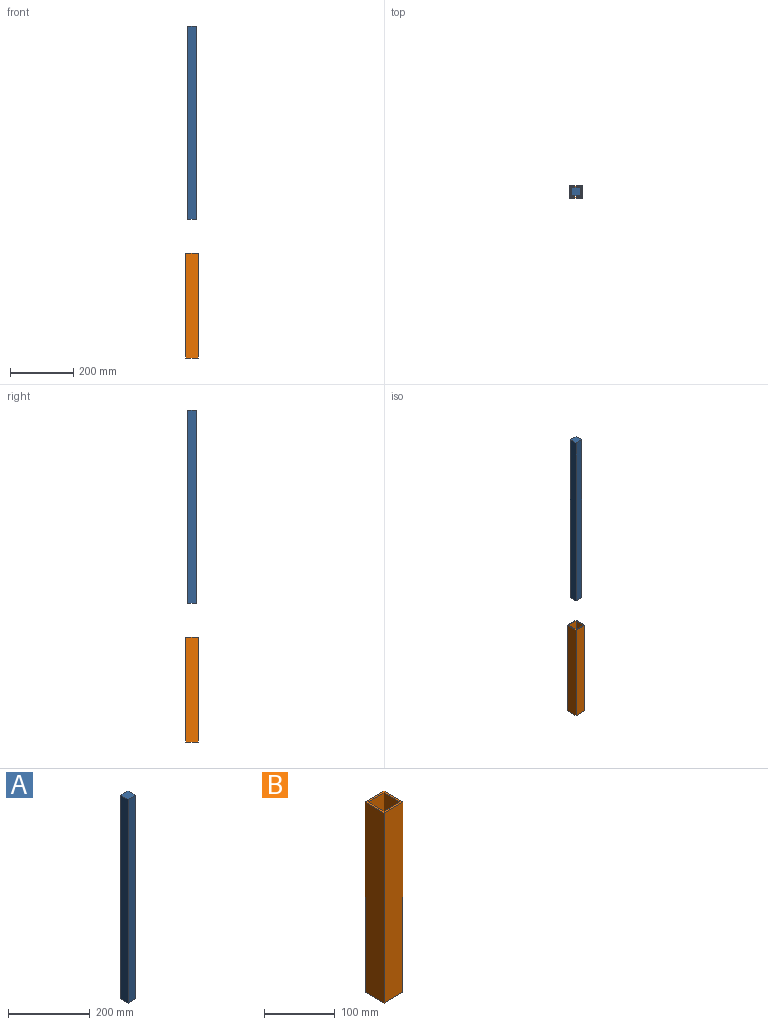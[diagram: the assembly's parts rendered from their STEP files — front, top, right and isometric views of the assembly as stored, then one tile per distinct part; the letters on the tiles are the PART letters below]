
ASSEMBLY  parts=2 mates=1
PART A: 6 faces, bbox 25.4x25.4x609.6 mm
  f0: plane 609.6x25.4mm, normal (0,1,0), area 15483.8mm2, adj f1,f3,f4,f5
  f1: plane 609.6x25.4mm, normal (-1,0,0), area 15483.8mm2, adj f0,f2,f4,f5
  f2: plane 609.6x25.4mm, normal (0,-1,0), area 15483.8mm2, adj f1,f3,f4,f5
  f3: plane 609.6x25.4mm, normal (1,0,0), area 15483.8mm2, adj f0,f2,f4,f5
  f4: plane 25.4x25.4mm, normal (0,0,1), area 645.2mm2, adj f0,f1,f2,f3
  f5: plane 25.4x25.4mm, normal (0,0,-1), area 645.2mm2, adj f0,f1,f2,f3
PART B: 10 faces, bbox 38.1x38.1x330.2 mm
  f0: plane 330.2x38.1mm, normal (0,1,0), area 12580.6mm2, adj f1,f7,f8,f9
  f1: plane 330.2x38.1mm, normal (-1,0,0), area 12580.6mm2, adj f0,f2,f8,f9
  f2: plane 330.2x38.1mm, normal (0,-1,0), area 12580.6mm2, adj f1,f7,f8,f9
  f3: plane 330.2x31.75mm, normal (1,0,0), area 10483.8mm2, adj f4,f6,f8,f9
  f4: plane 330.2x31.75mm, normal (0,-1,0), area 10483.8mm2, adj f3,f5,f8,f9
  f5: plane 330.2x31.75mm, normal (-1,0,0), area 10483.8mm2, adj f4,f6,f8,f9
  f6: plane 330.2x31.75mm, normal (0,1,0), area 10483.8mm2, adj f3,f5,f8,f9
  f7: plane 330.2x38.1mm, normal (1,0,0), area 12580.6mm2, adj f0,f2,f8,f9
  f8: plane 38.1x38.1mm, normal (0,0,1), area 443.5mm2, adj f0,f1,f2,f3,f4,f5,f6,f7
  f9: plane 38.1x38.1mm, normal (0,0,-1), area 443.5mm2, adj f0,f1,f2,f3,f4,f5,f6,f7
PLACE A t=(-50.75,0.53,-87.78)mm
PLACE B t=(-50.75,0.53,-524.38)mm
MATE slider B.f8 <-> A.f5  axis (0,0,1) through (-50.75,0.53,-194.18)mm
